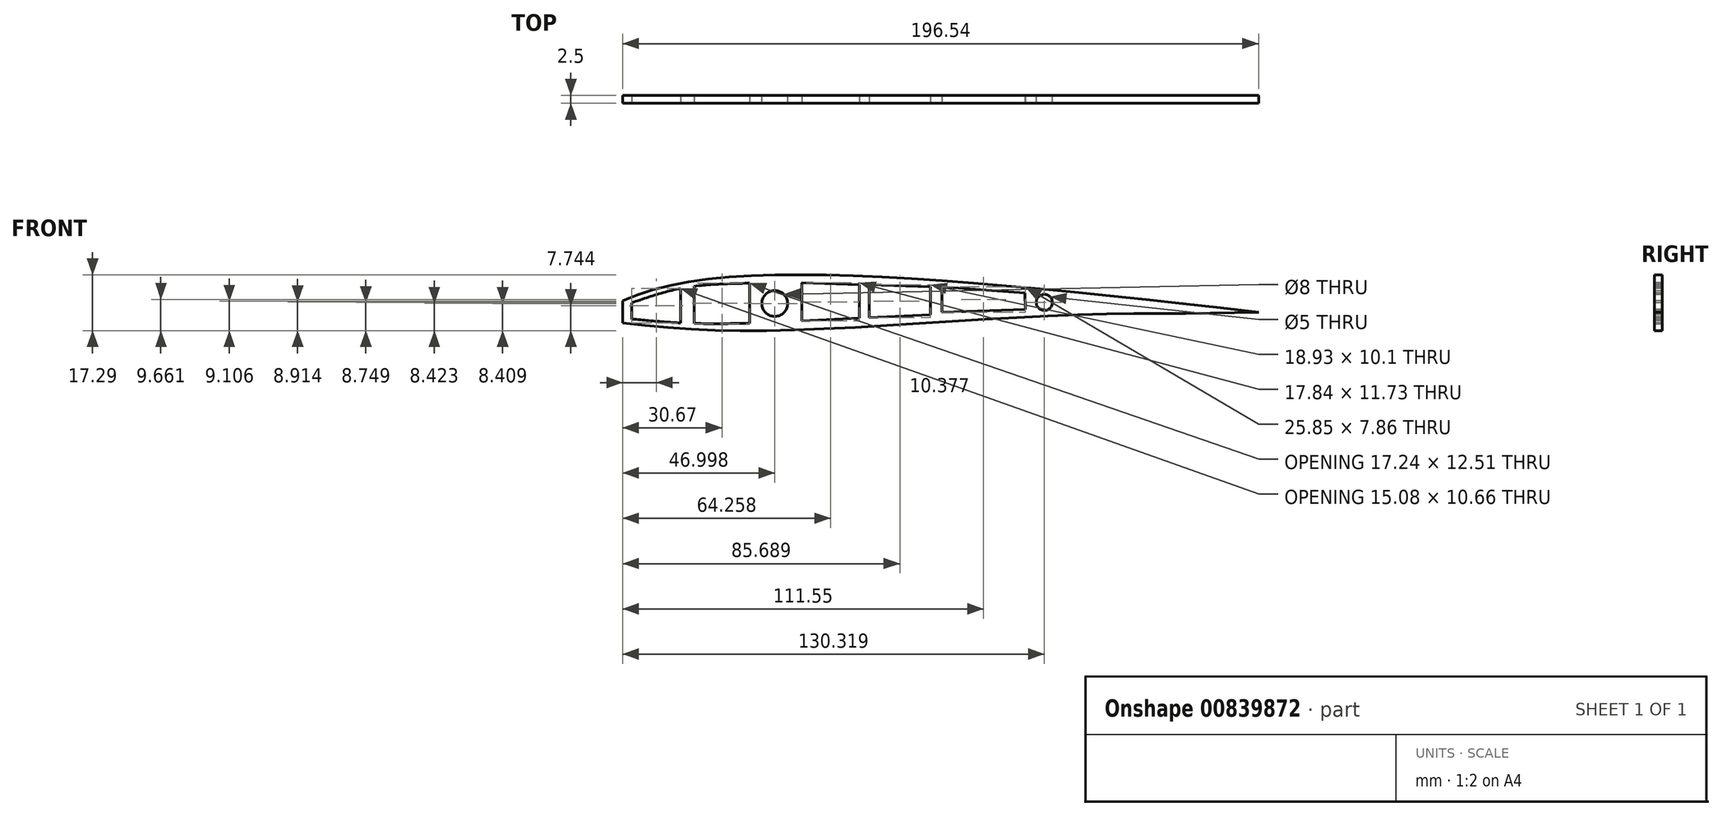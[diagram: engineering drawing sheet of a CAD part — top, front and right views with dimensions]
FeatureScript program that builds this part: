
annotation { "Feature Type Name" : "Feature", "Feature Type Description" : "" }
export const myFeature = defineFeature(function(context is Context, id is Id, definition is map)
    precondition{}
    {
        {
            var Q0;
            Q0=qCreatedBy(makeId("Front.planeOp"),FACE);
            var sketch = newSketch(context, id + "F0", { "sketchPlane" : qUnion([Q0])});
            skPoint(sketch, "E0.middle", {"position": v(0, 0) * mm});
            skLineSegment(sketch, "E1", {"start": v(-99.95, -4.05) * mm, "end": v(-99.64, -4.05) * mm});
            skFitSpline(sketch, "E2", {"points": [v(-96.98, -0.81) * mm, v(-45.24, 7.5) * mm, v(100, -4.05) * mm], "startDerivative": vector(97.58, 47.67) * mm, "endDerivative": vector(275.05, -31.29) * mm});
            skFitSpline(sketch, "E3", {"points": [v(-96.54, -7.34) * mm, v(-44.56, -9.6) * mm, v(41.7, -4.97) * mm, v(100, -4.05) * mm], "startDerivative": vector(159.07, -20.98) * mm, "endDerivative": vector(169.88, 6) * mm});
            skFitSpline(sketch, "E4", {"points": [v(-96.54, -7.34) * mm, v(-101.41, -5) * mm, v(-96.98, -0.81) * mm], "startDerivative": vector(-18.7, 3.9) * mm, "endDerivative": vector(17.62, 9.13) * mm});
            skArc(sketch, "E5.trimOffspring", {"start": v(-97.54, -7.12) * mm, "mid": v(-97.05, -7.27) * mm, "end": v(-96.54, -7.34) * mm});
            skFitSpline(sketch, "E6", {"points": [v(-96.34, -1.64) * mm, v(-45.34, 6.27) * mm, v(86.1, -3.38) * mm], "startDerivative": vector(82.57, 38.4) * mm, "endDerivative": vector(239.73, -24.74) * mm});
            skFitSpline(sketch, "E7", {"points": [v(-97.38, -6.05) * mm, v(-44.49, -7.96) * mm, v(41.39, -3.9) * mm, v(86.1, -3.38) * mm], "startDerivative": vector(144.05, -26.77) * mm, "endDerivative": vector(139.27, -2.3) * mm});
            skFitSpline(sketch, "E8", {"points": [v(-97.38, -6.05) * mm, v(-99.95, -4.56) * mm, v(-96.34, -1.64) * mm], "startDerivative": vector(-8.62, 1.03) * mm, "endDerivative": vector(10.24, 4.38) * mm});
            skSolve(sketch);
        }
        {
            var Q0;
            Q0=qCreatedBy(makeId("Front.planeOp"),FACE);
            var sketch = newSketch(context, id + "F1", { "sketchPlane" : qUnion([Q0])});
            skLineSegment(sketch, "E9", {"start": v(-109.84, -5.04) * mm, "end": v(108.45, -3.99) * mm});
            skCircle(sketch, "E10", {"center": v(-49.54, -1.37) * mm, "radius": 4 * mm});
            skCircle(sketch, "E11", {"center": v(33.78, -1.03) * mm, "radius": 2.5 * mm});
            skSolve(sketch);
        }
        {
            var Q0;
            {var subQ0=sQuery(id+"F0.wireOp",EDGE,"E6");Q0=makeQuery(id+"F0.imprint","IMPRINT",FACE,{"disambiguationData":[TD([[makeQuery(id+"F0.imprint","IMPRINT",EDGE,{"derivedFrom":subQ0}),-1.0]])]});}
            var Q1;
            {var subQ1=sQuery(id+"F0.wireOp",EDGE,"E2");Q1=makeQuery(id+"F0.imprint","IMPRINT",FACE,{"disambiguationData":[TD([[makeQuery(id+"F0.imprint","IMPRINT",EDGE,{"derivedFrom":subQ1}),-1.0]])]});}
            var Q2;
            Q2=makeQuery(id+"F1.imprint","IMPRINT",FACE,{"disambiguationData":[TD([[makeQuery(id+"F1.imprint","IMPRINT",EDGE,{"derivedFrom":sQuery(id+"F1.wireOp",EDGE,"E11")}),1.0]])]});
            var Q3;
            {var subQ0=sQuery(id+"F1.wireOp",EDGE,"E10");var subQ1=sQuery(id+"F1.wireOp",EDGE,"E9");var subQ2=makeQuery(id+"F1.imprint","INTERSECT",VERTEX,{"disambiguationData":[OD(0.0)],"derivedFrom":[subQ1,subQ0]});Q3=makeQuery(id+"F1.imprint","IMPRINT",FACE,{"disambiguationData":[TD([[makeQuery(id+"F1.imprint","IMPRINT",EDGE,{"disambiguationData":[TD([[subQ2,-1.0]])],"derivedFrom":subQ1}),1.0]])]});}
            var Q4;
            {var subQ0=sQuery(id+"F1.wireOp",EDGE,"E10");var subQ1=sQuery(id+"F1.wireOp",EDGE,"E9");var subQ2=makeQuery(id+"F1.imprint","INTERSECT",VERTEX,{"disambiguationData":[OD(0.0)],"derivedFrom":[subQ1,subQ0]});Q4=makeQuery(id+"F1.imprint","IMPRINT",FACE,{"disambiguationData":[TD([[makeQuery(id+"F1.imprint","IMPRINT",EDGE,{"disambiguationData":[TD([[subQ2,-1.0]])],"derivedFrom":subQ1}),-1.0]])]});}
            var Q5;
            {var subQ0=sQuery(id+"F0.wireOp",EDGE,"E5.trimOffspring");Q5=makeQuery(id+"F0.imprint","IMPRINT",FACE,{"disambiguationData":[TD([[makeQuery(id+"F0.imprint","IMPRINT",EDGE,{"derivedFrom":subQ0}),1.0]])]});}
            extrude(context, id + "F2", {"entities" : qUnion([Q0, Q1, Q2, Q3, Q4, Q5]), "depth" : 2.5 * mm, "offsetDistance" : 25 * mm});
        }
        {
            var Q0;
            Q0=qSketchRegion(id+"F1",true);
            var Q1;
            Q1=sQuery(id+"F1.wireOp",EDGE,"E11");
            var Q2;
            Q2=sQuery(id+"F1.wireOp",EDGE,"E10");
            extrude(context, id + "F3", {"entities" : qUnion([Q0]), "operationType" : NewBodyOperationType.REMOVE, "surfaceEntities" : qUnion([Q1, Q2]), "depth" : 2.5 * mm, "offsetDistance" : 25 * mm});
        }
        {
            var Q0;
            Q0=makeQuery(id+"F2.opExtrude","CAP_FACE",FACE,{"disambiguationData":[OSD([sQuery(id+"F0.wireOp",EDGE,"E2"),sQuery(id+"F0.wireOp",EDGE,"E3"),sQuery(id+"F0.wireOp",EDGE,"E4"),sQuery(id+"F0.wireOp",EDGE,"E5.trimOffspring")])],"isStart":false});
            var sketch = newSketch(context, id + "F4", { "sketchPlane" : qUnion([Q0])});
            skLineSegment(sketch, "E12", {"start": v(-96.54, -0.6) * mm, "end": v(-96.54, -7.34) * mm});
            skPoint(sketch, "E13.end.orphan", {"position": v(-96.98, -7.34) * mm});
            skLineSegment(sketch, "E14", {"start": v(-57.25, 4.9) * mm, "end": v(-57.25, -7.48) * mm});
            skFitSpline(sketch, "E15", {"points": [v(-57.25, -7.48) * mm, v(-75.97, -7.48) * mm, v(-93.7, -6.2) * mm], "startDerivative": vector(-37.23, -0.66) * mm, "endDerivative": vector(-35.67, 3.25) * mm});
            skFitSpline(sketch, "E16", {"points": [v(-57.25, 4.9) * mm, v(-77.46, 3.51) * mm, v(-93.7, -1.14) * mm], "startDerivative": vector(-39.88, -0.8) * mm, "endDerivative": vector(-32.92, -11.45) * mm});
            skLineSegment(sketch, "E17", {"start": v(-93.7, -1.14) * mm, "end": v(-93.7, -6.2) * mm});
            skLineSegment(sketch, "E18", {"start": v(-41.2, 5) * mm, "end": v(-41.2, -6.73) * mm});
            skLineSegment(sketch, "E19", {"start": v(-41.2, -6.73) * mm, "end": v(-23.36, -5.87) * mm});
            skLineSegment(sketch, "E20", {"start": v(-1.38, -4.8) * mm, "end": v(-1.38, 3.8) * mm});
            skLineSegment(sketch, "E21", {"start": v(-1.38, 3.8) * mm, "end": v(-20.32, 4.37) * mm});
            skLineSegment(sketch, "E22", {"start": v(2.08, 3.8) * mm, "end": v(2.08, -4.05) * mm});
            skLineSegment(sketch, "E23", {"start": v(2.08, -4.05) * mm, "end": v(27.94, -3.22) * mm});
            skLineSegment(sketch, "E24", {"start": v(27.94, -3.22) * mm, "end": v(27.77, 1.91) * mm});
            skLineSegment(sketch, "E25", {"start": v(27.77, 1.91) * mm, "end": v(2.08, 3.8) * mm});
            skLineSegment(sketch, "E26", {"start": v(-23.36, 4.47) * mm, "end": v(-23.36, -5.87) * mm});
            skLineSegment(sketch, "E27", {"start": v(-20.32, 4.37) * mm, "end": v(-20.32, -5.72) * mm});
            skLineSegment(sketch, "E28.trimOffspring", {"start": v(-23.36, 4.47) * mm, "end": v(-41.2, 5) * mm});
            skLineSegment(sketch, "E29.trimOffspring", {"start": v(-20.32, -5.72) * mm, "end": v(-1.38, -4.8) * mm});
            skLineSegment(sketch, "E30", {"start": v(-78.62, 3.3) * mm, "end": v(-78.62, -7.37) * mm});
            skLineSegment(sketch, "E31", {"start": v(-74.49, 3.96) * mm, "end": v(-74.49, -7.53) * mm});
            skFitSpline(sketch, "E32.trimOffspring", {"points": [v(-57.25, 4.9) * mm, v(-77.46, 3.51) * mm, v(-93.7, -1.14) * mm], "startDerivative": vector(-39.88, -0.8) * mm, "endDerivative": vector(-32.92, -11.45) * mm});
            skSolve(sketch);
        }
        {
            var Q0;
            {var subQ0=sQuery(id+"F4.wireOp",EDGE,"E12");Q0=makeQuery(id+"F4.imprint","IMPRINT",FACE,{"disambiguationData":[TD([[makeQuery(id+"F4.imprint","IMPRINT",EDGE,{"derivedFrom":subQ0}),-1.0]])]});}
            extrude(context, id + "F5", {"entities" : qUnion([Q0]), "operationType" : NewBodyOperationType.REMOVE, "oppositeDirection" : true, "depth" : 2.5 * mm, "offsetDistance" : 25 * mm});
        }
        {
            var Q0;
            Q0=makeQuery(id+"F4.imprint","IMPRINT",FACE,{"disambiguationData":[TD([[makeQuery(id+"F4.imprint","IMPRINT",EDGE,{"derivedFrom":sQuery(id+"F4.wireOp",EDGE,"E14")}),-1.0]])]});
            var Q1;
            Q1=makeQuery(id+"F4.imprint","IMPRINT",FACE,{"disambiguationData":[TD([[makeQuery(id+"F4.imprint","IMPRINT",EDGE,{"derivedFrom":sQuery(id+"F4.wireOp",EDGE,"E18")}),1.0]])]});
            var Q2;
            Q2=makeQuery(id+"F4.imprint","IMPRINT",FACE,{"disambiguationData":[TD([[makeQuery(id+"F4.imprint","IMPRINT",EDGE,{"derivedFrom":sQuery(id+"F4.wireOp",EDGE,"E22")}),1.0]])]});
            extrude(context, id + "F6", {"entities" : qUnion([Q0, Q1, Q2]), "operationType" : NewBodyOperationType.REMOVE, "oppositeDirection" : true, "depth" : 2.5 * mm, "offsetDistance" : 25 * mm});
        }
        {
            var Q0;
            Q0=makeQuery(id+"F4.imprint","IMPRINT",FACE,{"disambiguationData":[TD([[makeQuery(id+"F4.imprint","IMPRINT",EDGE,{"derivedFrom":sQuery(id+"F4.wireOp",EDGE,"E20")}),1.0]])]});
            extrude(context, id + "F7", {"entities" : qUnion([Q0]), "operationType" : NewBodyOperationType.REMOVE, "oppositeDirection" : true, "depth" : 2.5 * mm, "offsetDistance" : 25 * mm});
        }
        {
            var Q0;
            Q0=makeQuery(id+"F4.imprint","IMPRINT",FACE,{"disambiguationData":[TD([[makeQuery(id+"F4.imprint","IMPRINT",EDGE,{"derivedFrom":sQuery(id+"F4.wireOp",EDGE,"E17")}),1.0]])]});
            extrude(context, id + "F8", {"entities" : qUnion([Q0]), "operationType" : NewBodyOperationType.REMOVE, "oppositeDirection" : true, "depth" : 2.5 * mm, "offsetDistance" : 25 * mm});
        }
    });
